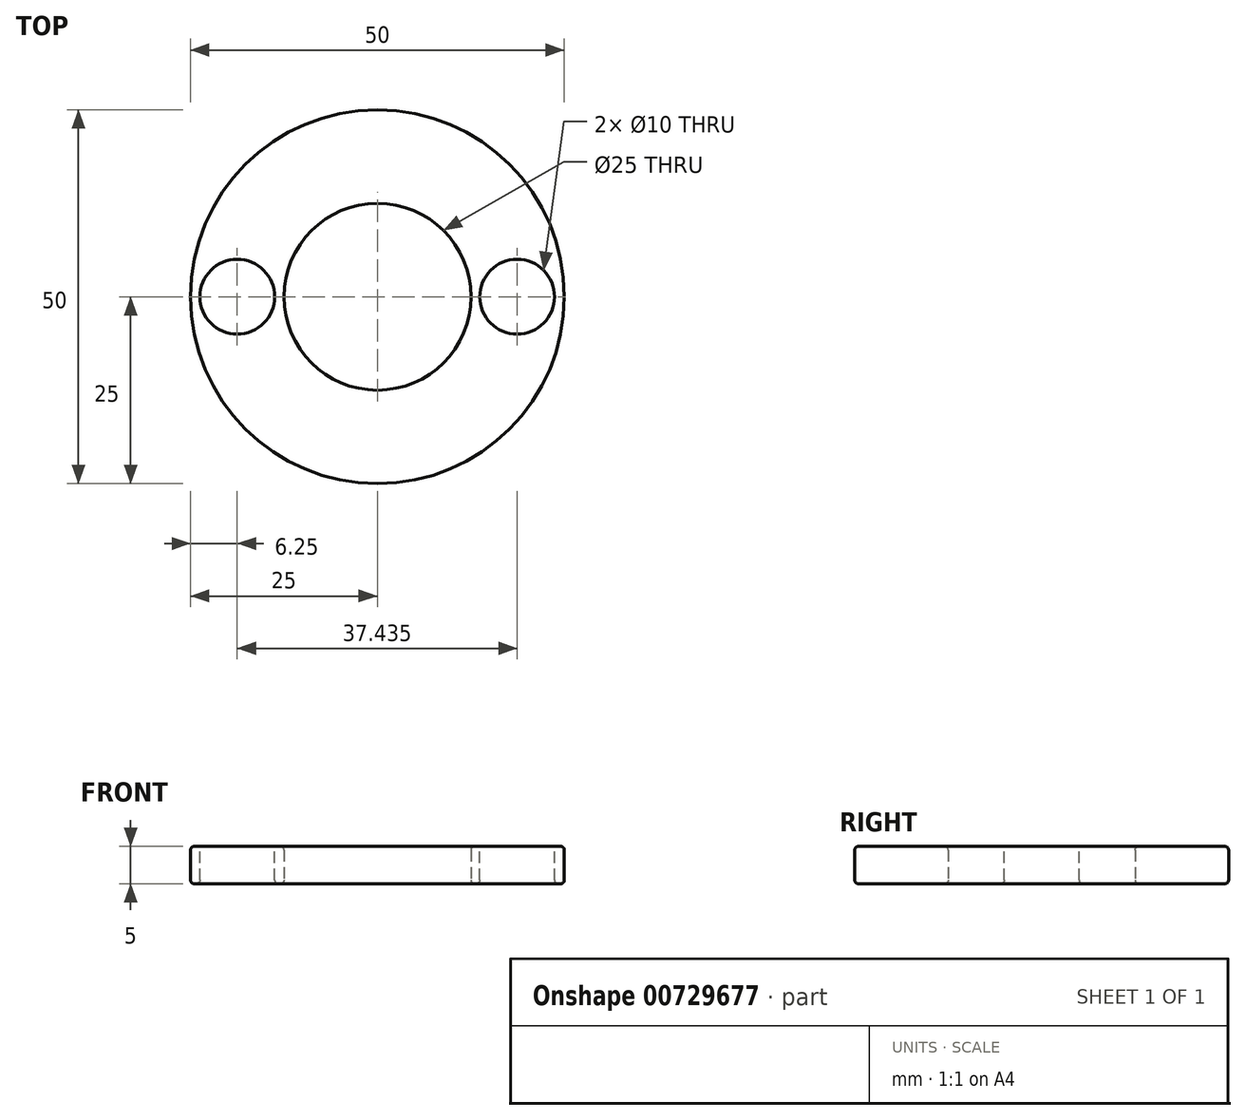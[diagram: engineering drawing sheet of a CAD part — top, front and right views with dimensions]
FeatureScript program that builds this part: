
annotation { "Feature Type Name" : "Feature", "Feature Type Description" : "" }
export const myFeature = defineFeature(function(context is Context, id is Id, definition is map)
    precondition{}
    {
        {
            var Q0;
            Q0=qCreatedBy(makeId("Top.planeOp"),FACE);
            var sketch = newSketch(context, id + "F0", { "sketchPlane" : qUnion([Q0])});
            skCircle(sketch, "E0", {"center": v(0, 0) * mm, "radius": 25 * mm});
            skCircle(sketch, "E1", {"center": v(0, 0) * mm, "radius": 12.5 * mm});
            skSolve(sketch);
        }
        {
            var Q0;
            Q0 = qSketchRegion(id + "F0", true);
            extrude(context, id + "F1", {"entities" : qUnion([Q0]), "depth" : 5 * mm, "offsetDistance" : 25 * mm});
        }
        {
            var Q0;
            Q0=makeQuery(id+"F1.opExtrude","CAP_FACE",FACE,{"disambiguationData":[OSD([sQuery(id+"F0.wireOp",EDGE,"E0"),sQuery(id+"F0.wireOp",EDGE,"E1")])],"isStart":false});
            var sketch = newSketch(context, id + "F2", { "sketchPlane" : qUnion([Q0])});
            skCircle(sketch, "E2", {"center": v(-18.75, 0) * mm, "radius": 5 * mm});
            skPoint(sketch, "E3.start.orphan", {"position": v(-25, 0) * mm});
            skPoint(sketch, "E4.trimOffspring.end.orphan", {"position": v(-12.5, 0) * mm});
            skLineSegment(sketch, "E5", {"start": v(12.5, 0) * mm, "end": v(25, 0) * mm});
            skPoint(sketch, "E6.center.orphan", {"position": v(18.69, 0) * mm});
            skCircle(sketch, "E7", {"center": v(18.69, 0) * mm, "radius": 5 * mm});
            skSolve(sketch);
        }
        {
            var Q0;
            Q0=makeQuery(id+"F2.imprint","IMPRINT",FACE,{"disambiguationData":[TD([[makeQuery(id+"F2.imprint","IMPRINT",EDGE,{"derivedFrom":sQuery(id+"F2.wireOp",EDGE,"E2")}),1.0]])]});
            var Q1;
            {var subQ0=sQuery(id+"F2.wireOp",EDGE,"E7");var subQ1=sQuery(id+"F2.wireOp",EDGE,"E5");var subQ2=makeQuery(id+"F2.imprint","INTERSECT",VERTEX,{"disambiguationData":[OD(0.0)],"derivedFrom":[subQ1,subQ0]});Q1=makeQuery(id+"F2.imprint","IMPRINT",FACE,{"disambiguationData":[TD([[makeQuery(id+"F2.imprint","IMPRINT",EDGE,{"disambiguationData":[TD([[subQ2,-1.0]])],"derivedFrom":subQ1}),-1.0]])]});}
            var Q2;
            {var subQ0=sQuery(id+"F2.wireOp",EDGE,"E7");var subQ1=sQuery(id+"F2.wireOp",EDGE,"E5");var subQ2=makeQuery(id+"F2.imprint","INTERSECT",VERTEX,{"disambiguationData":[OD(0.0)],"derivedFrom":[subQ1,subQ0]});Q2=makeQuery(id+"F2.imprint","IMPRINT",FACE,{"disambiguationData":[TD([[makeQuery(id+"F2.imprint","IMPRINT",EDGE,{"disambiguationData":[TD([[subQ2,-1.0]])],"derivedFrom":subQ1}),1.0]])]});}
            extrude(context, id + "F3", {"entities" : qUnion([Q0, Q1, Q2]), "operationType" : NewBodyOperationType.REMOVE, "oppositeDirection" : true, "depth" : 25 * mm, "offsetDistance" : 25 * mm});
        }
        {
            var Q0;
            Q0=makeQuery(id+"F1.opExtrude","CAP_EDGE",EDGE,{"disambiguationData":[OSD([sQuery(id+"F0.wireOp",EDGE,"E0")])],"isStart":false});
            var Q1;
            Q1=makeQuery(id+"F3.boolean.opBoolean","COPY",EDGE,{"derivedFrom":makeQuery(id+"F3.opExtrude","CAP_EDGE",EDGE,{"disambiguationData":[OSD([sQuery(id+"F2.wireOp",EDGE,"E2")])],"isStart":true})});
            var Q2;
            Q2=makeQuery(id+"F1.opExtrude","CAP_EDGE",EDGE,{"disambiguationData":[OSD([sQuery(id+"F0.wireOp",EDGE,"E1")])],"isStart":false});
            var Q3;
            Q3=makeQuery(id+"F3.boolean.opBoolean","COPY",EDGE,{"derivedFrom":makeQuery(id+"F3.opExtrude","CAP_EDGE",EDGE,{"disambiguationData":[OSD([sQuery(id+"F2.wireOp",EDGE,"E7")])],"isStart":true})});
            fillet(context, id + "F4", {"entities" : qUnion([Q0, Q1, Q2, Q3]), "radius" : 0.5 * mm, "tangentPropagation" : true, "allowEdgeOverflow" : false});
        }
        {
            var Q0;
            Q0=makeQuery(id+"F1.opExtrude","CAP_EDGE",EDGE,{"disambiguationData":[OSD([sQuery(id+"F0.wireOp",EDGE,"E0")])],"isStart":true});
            var Q1;
            Q1=makeQuery(id+"F1.opExtrude","CAP_EDGE",EDGE,{"disambiguationData":[OSD([sQuery(id+"F0.wireOp",EDGE,"E1")])],"isStart":true});
            var Q2;
            Q2=makeQuery(id+"F3.boolean.opBoolean","INTERSECT",EDGE,{"derivedFrom":[makeQuery(id+"F1.opExtrude","CAP_FACE",FACE,{"disambiguationData":[OSD([sQuery(id+"F0.wireOp",EDGE,"E0"),sQuery(id+"F0.wireOp",EDGE,"E1")])],"isStart":true}),makeQuery(id+"F3.opExtrude","SWEPT_FACE",FACE,{"disambiguationData":[OSD([sQuery(id+"F2.wireOp",EDGE,"E2")])]})]});
            var Q3;
            Q3=makeQuery(id+"F3.boolean.opBoolean","INTERSECT",EDGE,{"derivedFrom":[makeQuery(id+"F1.opExtrude","CAP_FACE",FACE,{"disambiguationData":[OSD([sQuery(id+"F0.wireOp",EDGE,"E0"),sQuery(id+"F0.wireOp",EDGE,"E1")])],"isStart":true}),makeQuery(id+"F3.opExtrude","SWEPT_FACE",FACE,{"disambiguationData":[OSD([sQuery(id+"F2.wireOp",EDGE,"E7")])]})]});
            fillet(context, id + "F5", {"entities" : qUnion([Q0, Q1, Q2, Q3]), "radius" : 0.5 * mm, "tangentPropagation" : true, "allowEdgeOverflow" : false});
        }
    });
